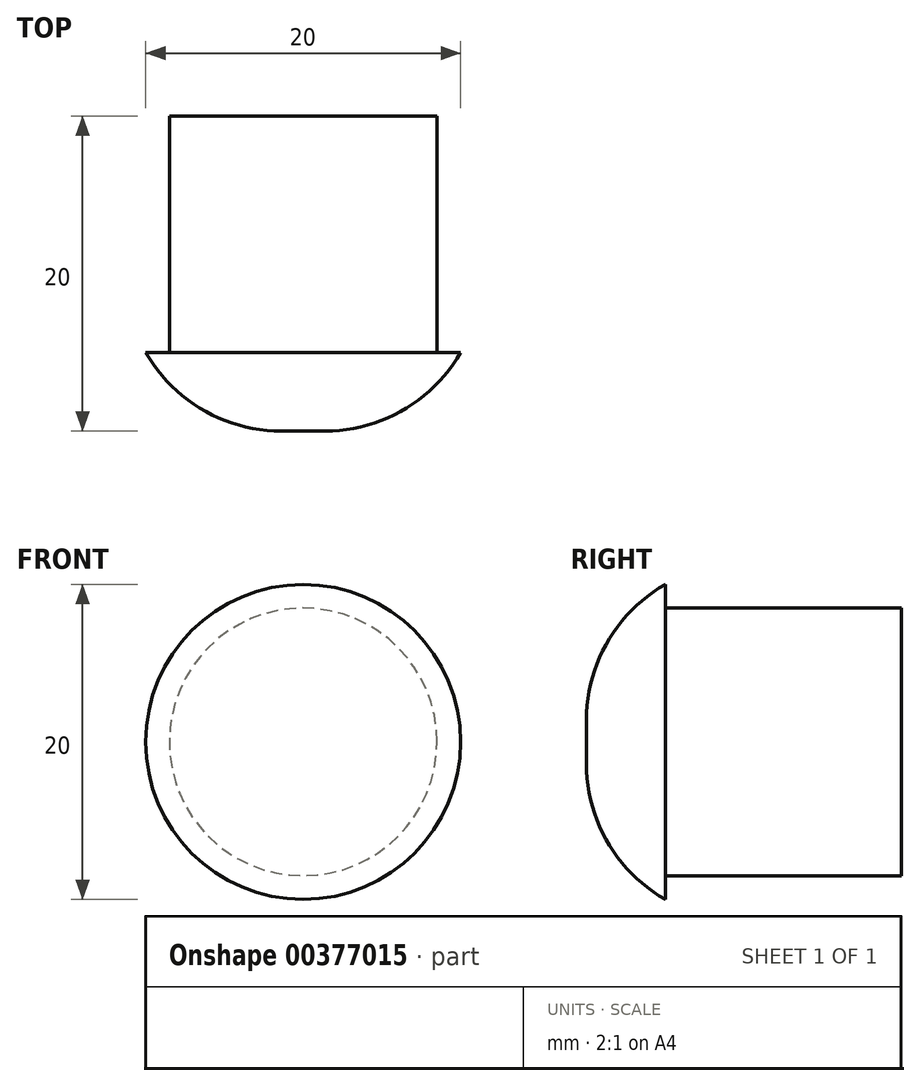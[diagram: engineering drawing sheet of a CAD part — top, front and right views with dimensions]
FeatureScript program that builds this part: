
annotation { "Feature Type Name" : "Feature", "Feature Type Description" : "" }
export const myFeature = defineFeature(function(context is Context, id is Id, definition is map)
    precondition{}
    {
        {
            var Q0;
            Q0=qCreatedBy(makeId("Front.planeOp"),FACE);
            var sketch = newSketch(context, id + "F0", { "sketchPlane" : qUnion([Q0])});
            skCircle(sketch, "E0", {"center": v(0, 0) * mm, "radius": 8.5 * mm});
            skSolve(sketch);
        }
        {
            var Q0;
            Q0 = qSketchRegion(id + "F0", true);
            extrude(context, id + "F1", {"entities" : qUnion([Q0]), "depth" : 15 * mm});
        }
        {
            var Q0;
            Q0=makeQuery(id+"F1.opExtrude","CAP_FACE",FACE,{"disambiguationData":[OSD([sQuery(id+"F0.wireOp",EDGE,"E0")])],"isStart":false});
            var sketch = newSketch(context, id + "F2", { "sketchPlane" : qUnion([Q0])});
            skCircle(sketch, "E1", {"center": v(0, 0) * mm, "radius": 10 * mm});
            skSolve(sketch);
        }
        {
            var Q0;
            Q0 = qSketchRegion(id + "F2", true);
            extrude(context, id + "F3", {"entities" : qUnion([Q0]), "operationType" : NewBodyOperationType.ADD, "depth" : 5 * mm});
        }
        {
            var Q0;
            Q0=makeQuery(id+"F3.opExtrude","CAP_EDGE",EDGE,{"disambiguationData":[OSD([sQuery(id+"F2.wireOp",EDGE,"E1")])],"isStart":false});
            fillet(context, id + "F4", {"entities" : qUnion([Q0]), "radius" : 9.9 * mm, "allowEdgeOverflow" : false});
        }
    });
